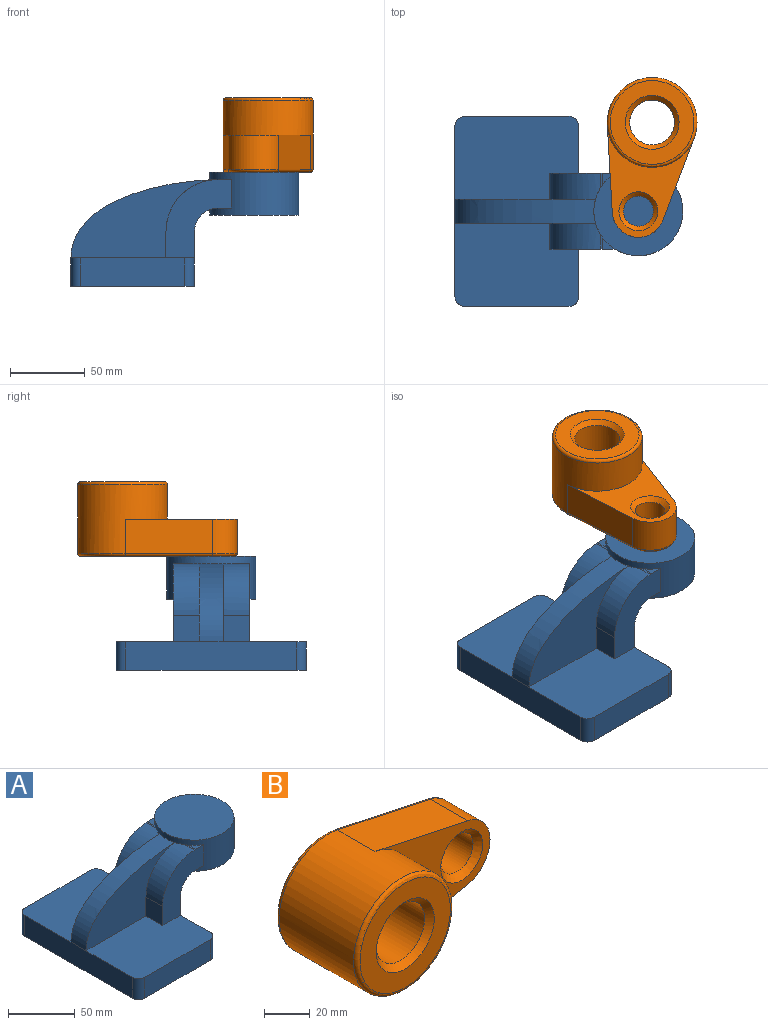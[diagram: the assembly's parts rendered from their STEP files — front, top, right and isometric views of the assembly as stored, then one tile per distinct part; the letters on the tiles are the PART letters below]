
ASSEMBLY  parts=2 mates=1
PART A: 30 faces, bbox 152.4x127x76.2 mm
  f0: plane 8.67x8.06mm, normal (0,0,1), area 30.2mm2, adj f1,f20,f23
  f1: extruded ~9.9x1.22mm, area 11mm2, adj f0,f6,f20,f23
  f2: extruded ~93.93x52.28mm, area 1848mm2, adj f9,f21,f22,f23
  f3: plane 8.67x8.06mm, normal (0,0,-1), area 30.2mm2, adj f17,f20,f23
  f4: plane 17.48x17.46mm, normal (-1,0,0), area 305.2mm2, adj f5,f6,f20,f22
  f5: plane 82.55x55.56mm, normal (0,0,1), area 4236.7mm2, adj f4,f8,f9,f12,f20,f22,f26,f27
  f6: cylinder r=34.92mm len=34.9mm, axis (0,1,0), area 922.7mm2, adj f1,f4,f20,f22,f23
  f7: plane 82.55x55.56mm, normal (0,0,1), area 4236.7mm2, adj f8,f9,f11,f16,f19,f21,f28,f29
  f8: plane 114.3x36.53mm, normal (1,0,0), area 3065.2mm2, adj f5,f7,f10,f17,f19,f20,f27,f29
  f9: plane 114.3x19.05mm, normal (-1,0,0), area 2177.4mm2, adj f2,f5,f7,f10,f26,f28
  f10: plane 127x82.55mm, normal (0,0,-1), area 10449.2mm2, adj f8,f9,f11,f12,f26,f27,f28,f29
  f11: plane 69.85x19.05mm, normal (0,-1,0), area 1330.6mm2, adj f7,f10,f28,f29
  f12: plane 69.85x19.05mm, normal (0,1,0), area 1330.6mm2, adj f5,f10,f26,f27
  f13: plane 8.67x8.06mm, normal (0,0,1), area 30.2mm2, adj f14,f19,f23
  f14: extruded ~9.9x1.22mm, area 11mm2, adj f13,f15,f19,f23
  f15: cylinder r=34.92mm len=34.9mm, axis (0,1,0), area 922.7mm2, adj f14,f16,f19,f21,f23
  f16: plane 17.48x17.46mm, normal (-1,0,0), area 305.2mm2, adj f7,f15,f19,f21
  f17: cylinder r=15.88mm len=50.8mm, axis (0,1,0), area 1133.4mm2, adj f3,f8,f18,f19,f20,f23
  f18: plane 8.67x8.06mm, normal (0,0,-1), area 30.2mm2, adj f17,f19,f23
  f19: plane 52.4x43.59mm, normal (0,-1,0), area 1258.1mm2, adj f7,f8,f13,f14,f15,f16,f17,f18
  f20: plane 52.4x43.59mm, normal (0,1,0), area 1258.1mm2, adj f0,f1,f3,f4,f5,f6,f8,f17
  f21: plane 98.43x52.4mm, normal (0,-1,0), area 2496.5mm2, adj f2,f7,f15,f16,f23
  f22: plane 98.43x52.4mm, normal (0,1,0), area 2496.5mm2, adj f2,f4,f5,f6,f23
  f23: cylinder r=29.77mm len=59.55mm, axis (0,0,-1), area 4171.5mm2, adj f0,f1,f2,f3,f6,f13,f14,f15
  f24: plane 59.55x59.55mm, normal (0,0,-1), area 2784.8mm2, adj f23
  f25: plane 59.55x59.55mm, normal (0,0,1), area 2784.8mm2, adj f23
  f26: cylinder r=6.35mm len=19.05mm, axis (0,0,-1), area 190mm2, adj f5,f9,f10,f12
  f27: cylinder r=6.35mm len=19.05mm, axis (0,0,1), area 190mm2, adj f5,f8,f10,f12
  f28: cylinder r=6.35mm len=19.05mm, axis (0,0,1), area 190mm2, adj f7,f9,f10,f11
  f29: cylinder r=6.35mm len=19.05mm, axis (0,0,-1), area 190mm2, adj f7,f8,f10,f11
PART B: 16 faces, bbox 111.4x50x64.9 mm
  f0: plane 71.25x58.68mm, normal (0,-1,0), area 1448.5mm2, adj f1,f2,f3,f4,f14
  f1: cylinder r=30mm len=60mm, axis (0,1,0), area 6792.7mm2, adj f0,f2,f4,f9,f11
  f2: plane 57.4x23mm, normal (0.21,0,-0.98), area 1349.7mm2, adj f0,f1,f3,f10
  f3: cylinder r=17.5mm len=34.23mm, axis (0,1,0), area 1095.5mm2, adj f0,f2,f4,f12
  f4: plane 57.4x23mm, normal (0.21,0,0.98), area 1349.7mm2, adj f0,f1,f3,f13
  f5: cylinder r=15mm len=47mm, axis (0,1,0), area 4429.6mm2, adj f7,f15
  f6: cylinder r=10mm len=22mm, axis (0,1,0), area 1382.3mm2, adj f7,f14
  f7: plane 103.5x56mm, normal (0,1,0), area 3254.7mm2, adj f5,f6,f10,f11,f12,f13
  f8: plane 56x56mm, normal (0,-1,0), area 1445.1mm2, adj f9,f15
  f9: torus R=28mm, axis (0,-1,0), area 577.8mm2, adj f1,f8
  f10: cylinder r=2mm len=57.81mm, axis (0.98,0,0.21), area 184.4mm2, adj f2,f7,f11,f12
  f11: torus R=28mm, axis (0,-1,0), area 327.5mm2, adj f1,f7,f10,f13
  f12: torus R=15.5mm, axis (0,-1,0), area 143.4mm2, adj f3,f7,f10,f13
  f13: cylinder r=2mm len=57.81mm, axis (-0.98,0,0.21), area 184.4mm2, adj f4,f7,f11,f12
  f14: cone r=10mm half-angle=45deg, axis (0,-1,0), area 306.6mm2, adj f0,f6
  f15: cone r=15mm half-angle=45deg, axis (0,-1,0), area 439.8mm2, adj f5,f8
PLACE A t=(-51.03,22.96,17.86)mm fixed
PLACE B rot(axis=(-0.52,0.6,-0.6),125.2deg) t=(41.76,82.25,84.54)mm
MATE revolute B.f3 <-> A.f23  axis (0,0,-1) through (32.57,22.96,84.54)mm
